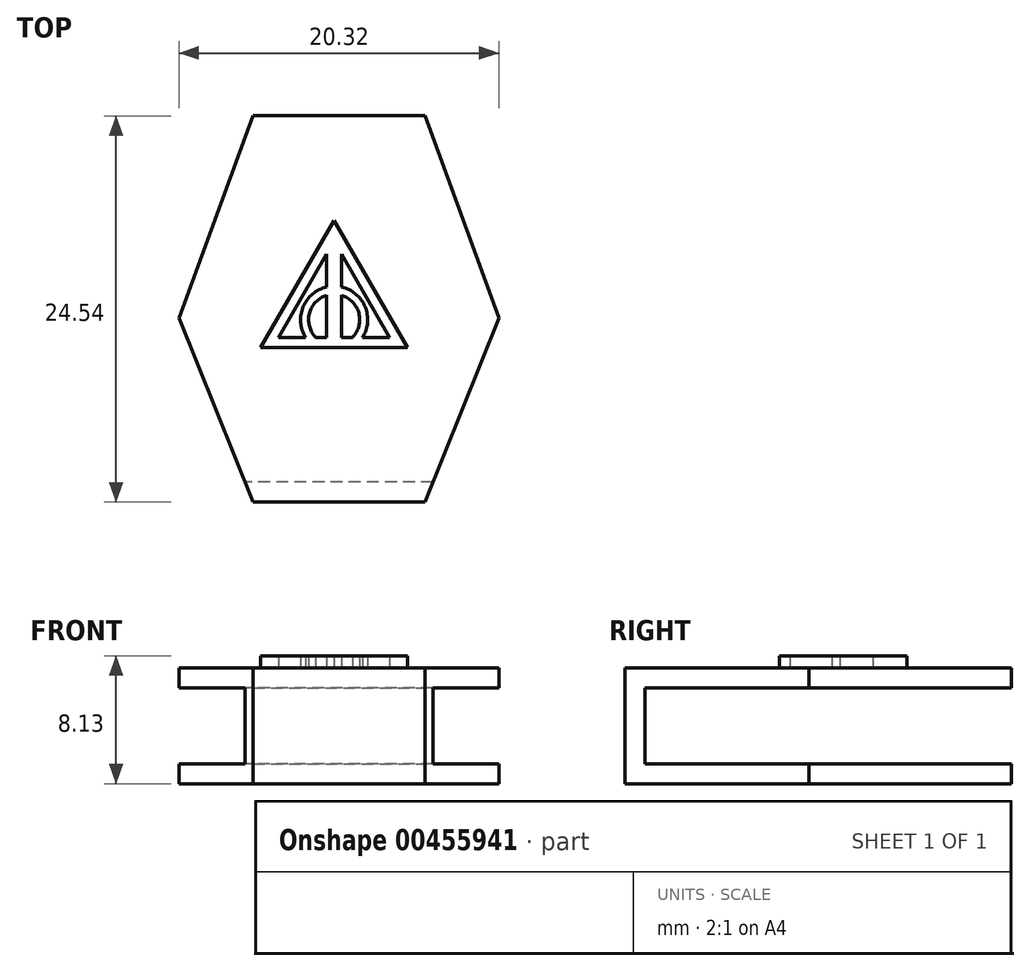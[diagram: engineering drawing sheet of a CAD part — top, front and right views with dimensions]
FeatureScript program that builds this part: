
annotation { "Feature Type Name" : "Feature", "Feature Type Description" : "" }
export const myFeature = defineFeature(function(context is Context, id is Id, definition is map)
    precondition{}
    {
        {
            var Q0;
            Q0=qCreatedBy(makeId("Top.planeOp"),FACE);
            var sketch = newSketch(context, id + "F0", { "sketchPlane" : qUnion([Q0])});
            skPoint(sketch, "E0.0.midPoint", {"position": v(-10.33, 10.69) * mm});
            skPoint(sketch, "E1.0.midPoint", {"position": v(-8.7, 28.2) * mm});
            skPoint(sketch, "E2.orphan", {"position": v(-6.93, 30.74) * mm});
            skPoint(sketch, "E1.0.end.orphan", {"position": v(-10.48, 25.65) * mm});
            skPoint(sketch, "E3.orphan", {"position": v(-12.14, 10.69) * mm});
            skPoint(sketch, "E4.orphan", {"position": v(-8.53, 10.69) * mm});
            skPoint(sketch, "E5.orphan", {"position": v(-8.53, 16.95) * mm});
            skPoint(sketch, "E0.cCircle.center.orphan", {"position": v(-10.33, 13.82) * mm});
            skPoint(sketch, "E0.3.end.orphan", {"position": v(-10.33, 16.95) * mm});
            skPoint(sketch, "E0.3.start.orphan", {"position": v(-12.14, 16.95) * mm});
            skLineSegment(sketch, "E6", {"start": v(2.9, 28.1) * mm, "end": v(14.4, 28.1) * mm});
            skLineSegment(sketch, "E7", {"start": v(14.4, 28.1) * mm, "end": v(19.1, 15.26) * mm});
            skLineSegment(sketch, "E8", {"start": v(19.1, 15.26) * mm, "end": v(14.4, 3.56) * mm});
            skLineSegment(sketch, "E9", {"start": v(14.4, 3.56) * mm, "end": v(3.47, 3.56) * mm});
            skLineSegment(sketch, "E10", {"start": v(8.93, 3.56) * mm, "end": v(8.93, 2.7) * mm});
            skPoint(sketch, "E10.startSnap0", {"position": v(8.93, 3.56) * mm});
            skPoint(sketch, "E10.endSnap0", {"position": v(8.93, 3.56) * mm});
            skPoint(sketch, "E11.start.orphan", {"position": v(-0.75, 15.26) * mm});
            skLineSegment(sketch, "E12.MirrorCS", {"start": v(3.47, 28.1) * mm, "end": v(-1.23, 15.26) * mm});
            skLineSegment(sketch, "E13.MirrorCS", {"start": v(-1.23, 15.26) * mm, "end": v(3.47, 3.56) * mm});
            skPoint(sketch, "E14.orphan", {"position": v(8.93, 34.43) * mm});
            skLineSegment(sketch, "E15", {"start": v(-1.23, 15.26) * mm, "end": v(-0.75, 15.26) * mm});
            skSolve(sketch);
        }
        {
            var Q0;
            {var subQ3=sQuery(id+"F0.wireOp",EDGE,"E7");Q0=makeQuery(id+"F0.imprint","IMPRINT",FACE,{"disambiguationData":[TD([[makeQuery(id+"F0.imprint","IMPRINT",EDGE,{"derivedFrom":subQ3}),-1.0]])]});}
            extrude(context, id + "F1", {"entities" : qUnion([Q0]), "depth" : 7.37 * mm});
        }
        {
            var Q0;
            Q0=makeQuery(id+"F1.opExtrude","SWEPT_FACE",FACE,{"disambiguationData":[OSD([sQuery(id+"F0.wireOp",EDGE,"E6")])]});
            var Q1;
            Q1=makeQuery(id+"F1.opExtrude","SWEPT_FACE",FACE,{"disambiguationData":[OSD([sQuery(id+"F0.wireOp",EDGE,"E7")])]});
            var Q2;
            Q2=makeQuery(id+"F1.opExtrude","SWEPT_FACE",FACE,{"disambiguationData":[OSD([sQuery(id+"F0.wireOp",EDGE,"E8")])]});
            var Q3;
            Q3=makeQuery(id+"F1.opExtrude","SWEPT_FACE",FACE,{"disambiguationData":[OSD([sQuery(id+"F0.wireOp",EDGE,"E12.MirrorCS")])]});
            var Q4;
            Q4=makeQuery(id+"F1.opExtrude","SWEPT_FACE",FACE,{"disambiguationData":[OSD([sQuery(id+"F0.wireOp",EDGE,"E13.MirrorCS")])]});
            shell(context, id + "F2", {"entities" : qUnion([Q0, Q1, Q2, Q3, Q4]), "thickness" : 1.27 * mm});
        }
        {
            var Q0;
            Q0=makeQuery(id+"F1.opExtrude","CAP_FACE",FACE,{"disambiguationData":[OSD([sQuery(id+"F0.wireOp",EDGE,"E6"),sQuery(id+"F0.wireOp",EDGE,"E7"),sQuery(id+"F0.wireOp",EDGE,"E8"),sQuery(id+"F0.wireOp",EDGE,"E9"),sQuery(id+"F0.wireOp",EDGE,"E12.MirrorCS"),sQuery(id+"F0.wireOp",EDGE,"E13.MirrorCS")])],"isStart":false});
            var sketch = newSketch(context, id + "F3", { "sketchPlane" : qUnion([Q0])});
            skLineSegment(sketch, "E16.0", {"start": v(13.3, 13.37) * mm, "end": v(3.96, 13.37) * mm});
            skLineSegment(sketch, "E16.1", {"start": v(3.96, 13.37) * mm, "end": v(8.63, 21.46) * mm});
            skLineSegment(sketch, "E16.2", {"start": v(8.63, 21.46) * mm, "end": v(13.3, 13.37) * mm});
            skPoint(sketch, "E16.0.midPoint", {"position": v(8.63, 13.37) * mm});
            skLineSegment(sketch, "E17.0", {"start": v(12.15, 14.03) * mm, "end": v(10.44, 14.03) * mm});
            skLineSegment(sketch, "E17.1", {"start": v(5.1, 14.03) * mm, "end": v(8.15, 19.3) * mm});
            skLineSegment(sketch, "E17.2", {"start": v(9.1, 19.3) * mm, "end": v(12.15, 14.03) * mm});
            skPoint(sketch, "E17.0.midPoint", {"position": v(8.63, 14.03) * mm});
            skLineSegment(sketch, "E18", {"start": v(8.15, 19.3) * mm, "end": v(8.15, 17.23) * mm});
            skLineSegment(sketch, "E19", {"start": v(9.1, 19.3) * mm, "end": v(9.1, 17.23) * mm});
            skArc(sketch, "E20", {"start": v(10.44, 14.03) * mm, "mid": v(10.6, 15.97) * mm, "end": v(9.1, 17.23) * mm});
            skArc(sketch, "E21", {"start": v(9.8, 14.03) * mm, "mid": v(10.2, 15.56) * mm, "end": v(9.1, 16.7) * mm});
            skPoint(sketch, "E17.cCircle.center.orphan", {"position": v(8.63, 16.07) * mm});
            skArc(sketch, "E22.trimOffspring", {"start": v(8.15, 16.7) * mm, "mid": v(7.06, 15.56) * mm, "end": v(7.45, 14.03) * mm});
            skArc(sketch, "E23.trimOffspring", {"start": v(8.15, 17.23) * mm, "mid": v(6.66, 15.97) * mm, "end": v(6.81, 14.03) * mm});
            skLineSegment(sketch, "E24.trimOffspring", {"start": v(6.81, 14.03) * mm, "end": v(5.1, 14.03) * mm});
            skLineSegment(sketch, "E25.trimOffspring", {"start": v(9.8, 14.03) * mm, "end": v(9.1, 14.03) * mm});
            skLineSegment(sketch, "E26.trimOffspring", {"start": v(9.1, 16.7) * mm, "end": v(9.1, 14.03) * mm});
            skLineSegment(sketch, "E27.trimOffspring", {"start": v(8.15, 16.7) * mm, "end": v(8.15, 14.03) * mm});
            skLineSegment(sketch, "E28.trimOffspring", {"start": v(8.15, 14.03) * mm, "end": v(7.45, 14.03) * mm});
            skSolve(sketch);
        }
        {
            var Q0;
            Q0=makeQuery(id+"F3.imprint","IMPRINT",FACE,{"disambiguationData":[TD([[makeQuery(id+"F3.imprint","IMPRINT",EDGE,{"derivedFrom":sQuery(id+"F3.wireOp",EDGE,"E16.0")}),-1.0]])]});
            extrude(context, id + "F4", {"entities" : qUnion([Q0]), "operationType" : NewBodyOperationType.ADD, "depth" : 0.76 * mm});
        }
    });
